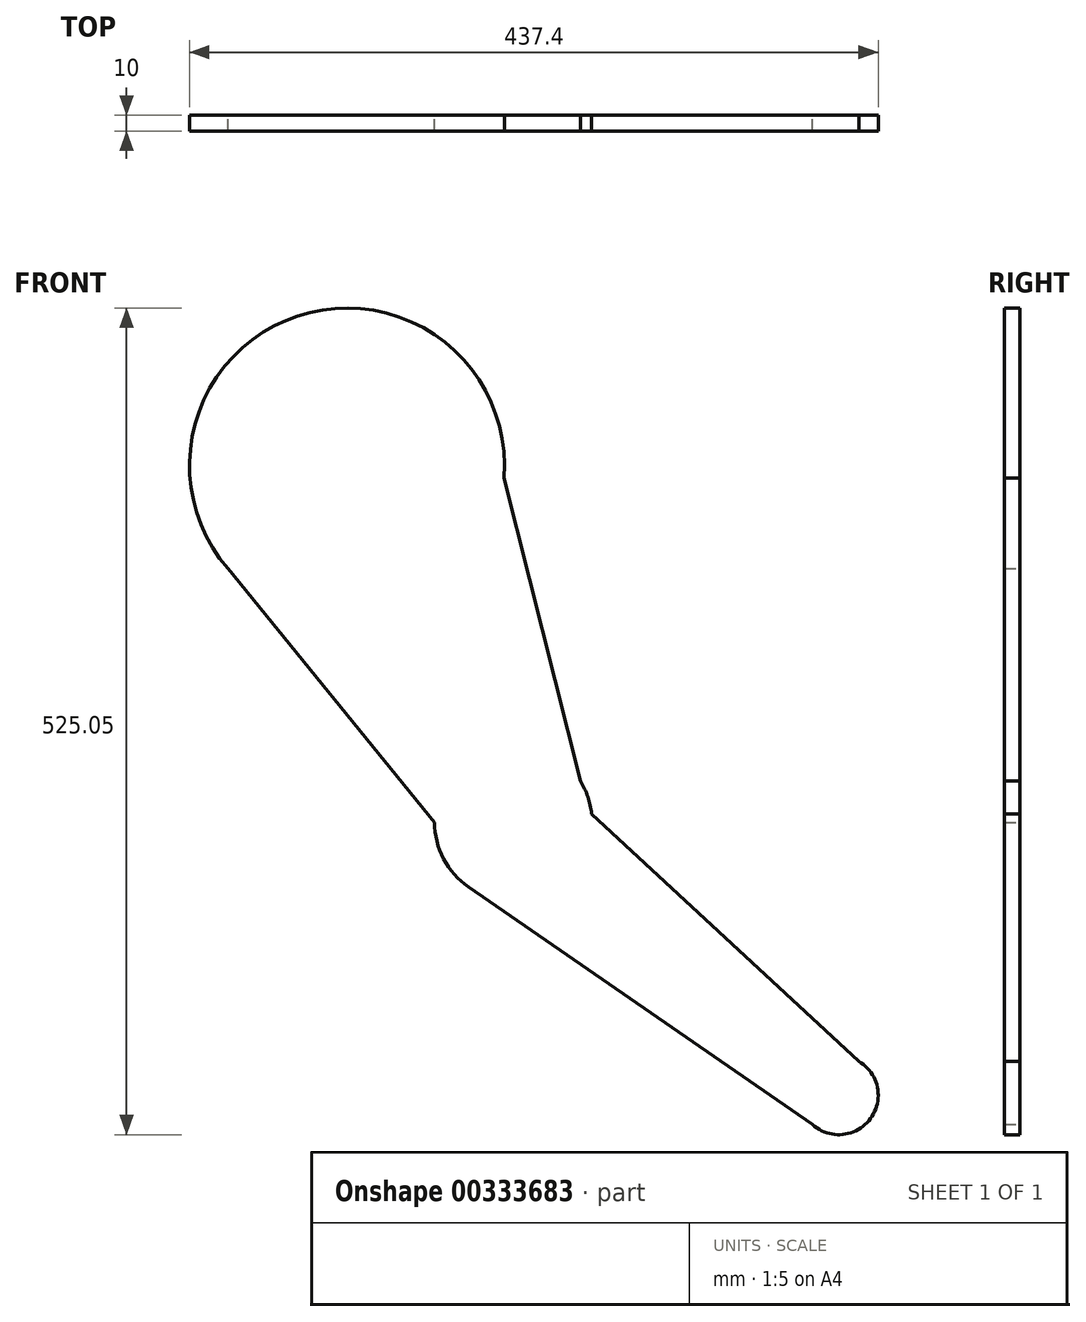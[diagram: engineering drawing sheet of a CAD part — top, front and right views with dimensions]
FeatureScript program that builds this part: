
annotation { "Feature Type Name" : "Feature", "Feature Type Description" : "" }
export const myFeature = defineFeature(function(context is Context, id is Id, definition is map)
    precondition{}
    {
        {
            var Q0;
            Q0=qCreatedBy(makeId("Front.planeOp"),FACE);
            var sketch = newSketch(context, id + "F0", { "sketchPlane" : qUnion([Q0])});
            skArc(sketch, "E0", {"start": v(99.69, -7.93) * mm, "mid": v(-31.25, 95) * mm, "end": v(-75.5, -65.57) * mm});
            skLineSegment(sketch, "E1", {"start": v(0, 0) * mm, "end": v(0, -121.37) * mm, "construction": true});
            skArc(sketch, "E2", {"start": v(55.65, -226.58) * mm, "mid": v(61.38, -249.8) * mm, "end": v(77.23, -267.71) * mm});
            skLineSegment(sketch, "E3", {"start": v(105.65, -276.58) * mm, "end": v(105.65, -287.35) * mm, "construction": true});
            skArc(sketch, "E4", {"start": v(295.67, -418.64) * mm, "mid": v(332.56, -414.83) * mm, "end": v(325.08, -378.51) * mm});
            skLineSegment(sketch, "E5", {"start": v(-79.48, -60.68) * mm, "end": v(55.65, -226.58) * mm});
            skPoint(sketch, "E5.startSnap0", {"position": v(0, -60.68) * mm});
            skLineSegment(sketch, "E6", {"start": v(99.69, -7.93) * mm, "end": v(148.27, -200.43) * mm});
            skLineSegment(sketch, "E7", {"start": v(295.67, -418.64) * mm, "end": v(77.23, -267.71) * mm});
            skLineSegment(sketch, "E8", {"start": v(325.08, -378.51) * mm, "end": v(155.37, -221.25) * mm});
            skArc(sketch, "E9.trimOffspring", {"start": v(155.37, -221.25) * mm, "mid": v(152.98, -210.44) * mm, "end": v(148.27, -200.43) * mm});
            skSolve(sketch);
        }
        {
            var Q0;
            Q0 = qSketchRegion(id + "F0", true);
            extrude(context, id + "F1", {"entities" : qUnion([Q0]), "depth" : 10 * mm});
        }
    });
